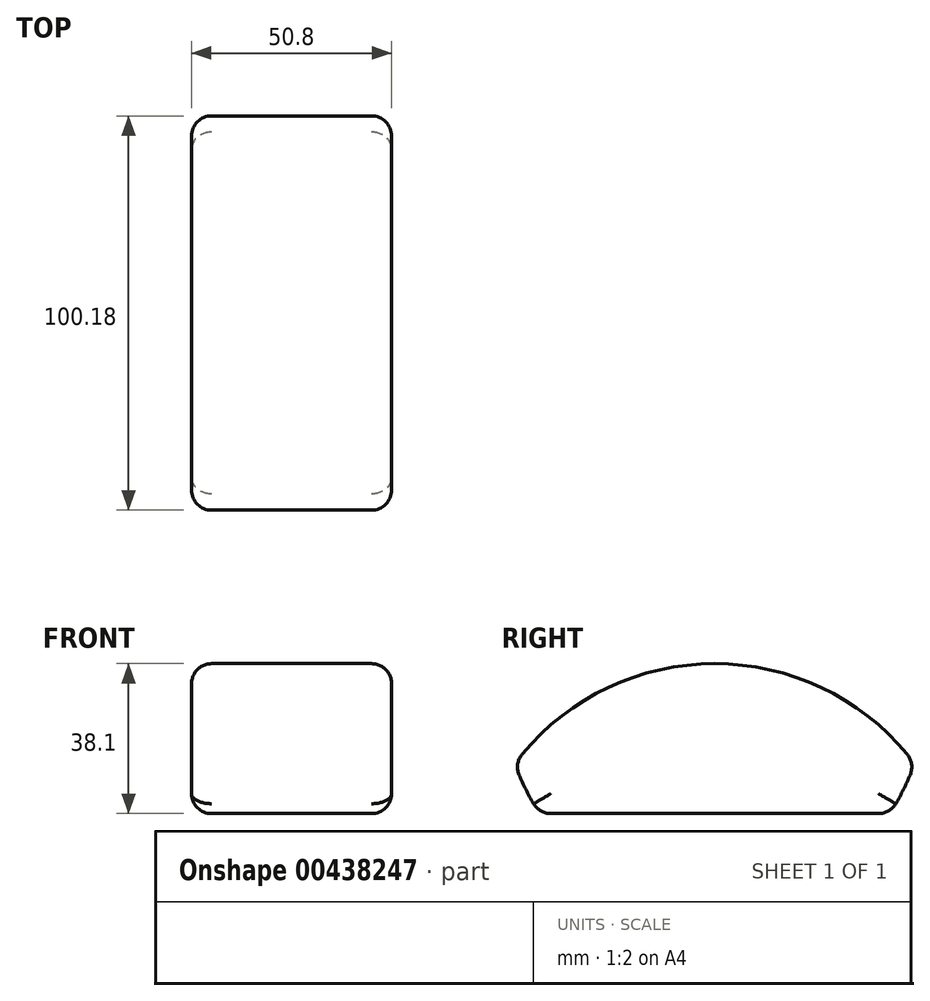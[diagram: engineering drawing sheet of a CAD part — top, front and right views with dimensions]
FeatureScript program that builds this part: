
annotation { "Feature Type Name" : "Feature", "Feature Type Description" : "" }
export const myFeature = defineFeature(function(context is Context, id is Id, definition is map)
    precondition{}
    {
        {
            var Q0;
            Q0=qCreatedBy(makeId("Right.planeOp"),FACE);
            var sketch = newSketch(context, id + "F0", { "sketchPlane" : qUnion([Q0])});
            skLineSegment(sketch, "E0", {"start": v(0, 0) * mm, "end": v(0, -12.7) * mm});
            skLineSegment(sketch, "E1", {"start": v(0, -12.7) * mm, "end": v(-44.45, -12.7) * mm});
            skLineSegment(sketch, "E2", {"start": v(0, -12.7) * mm, "end": v(44.45, -12.7) * mm});
            skLineSegment(sketch, "E3", {"start": v(0, 0) * mm, "end": v(-50.8, 0) * mm});
            skLineSegment(sketch, "E4", {"start": v(0, 0) * mm, "end": v(50.8, 0) * mm});
            skArc(sketch, "E5", {"start": v(-50.8, 0) * mm, "mid": v(-47.98, -6.53) * mm, "end": v(-44.45, -12.7) * mm});
            skArc(sketch, "E6", {"start": v(44.45, -12.7) * mm, "mid": v(47.98, -6.53) * mm, "end": v(50.8, 0) * mm});
            skLineSegment(sketch, "E7", {"start": v(0, 0) * mm, "end": v(0, 25.4) * mm});
            skLineSegment(sketch, "E8", {"start": v(50.8, 0) * mm, "end": v(6.35, 0) * mm});
            skArc(sketch, "E9", {"start": v(6.35, 0) * mm, "mid": v(4.15, 12.94) * mm, "end": v(0, 25.4) * mm});
            skArc(sketch, "E10", {"start": v(50.8, 0) * mm, "mid": v(28.4, 18.7) * mm, "end": v(0, 25.4) * mm});
            skArc(sketch, "E11", {"start": v(0, 25.4) * mm, "mid": v(-28.4, 18.7) * mm, "end": v(-50.8, 0) * mm});
            skSolve(sketch);
        }
        {
            var Q0;
            Q0 = qSketchRegion(id + "F0", true);
            extrude(context, id + "F1", {"entities" : qUnion([Q0]), "depth" : 25.4 * mm});
        }
        {
            var Q0;
            Q0 = qSketchRegion(id + "F0", true);
            extrude(context, id + "F2", {"entities" : qUnion([Q0]), "operationType" : NewBodyOperationType.ADD, "oppositeDirection" : true, "depth" : 25.4 * mm});
        }
        {
            var Q0;
            {var subQ0=sQuery(id+"F0.wireOp",EDGE,"E6");Q0=makeQuery(id+"F2.boolean.opBoolean","MERGE",FACE,{"derivedFrom":[makeQuery(id+"F1.opExtrude","SWEPT_FACE",FACE,{"disambiguationData":[OSD([subQ0])]}),makeQuery(id+"F2.opExtrude","SWEPT_FACE",FACE,{"disambiguationData":[OSD([subQ0])]})]});}
            var Q1;
            {var subQ0=sQuery(id+"F0.wireOp",EDGE,"E11");var subQ1=sQuery(id+"F0.wireOp",EDGE,"E10");Q1=makeQuery(id+"F2.boolean.opBoolean","MERGE",FACE,{"derivedFrom":[makeQuery(id+"F1.opExtrude","SWEPT_FACE",FACE,{"disambiguationData":[OSD([subQ1,subQ0])]}),makeQuery(id+"F2.opExtrude","SWEPT_FACE",FACE,{"disambiguationData":[OSD([subQ1,subQ0])]})]});}
            var Q2;
            {var subQ0=sQuery(id+"F0.wireOp",EDGE,"E5");Q2=makeQuery(id+"F2.boolean.opBoolean","MERGE",FACE,{"derivedFrom":[makeQuery(id+"F1.opExtrude","SWEPT_FACE",FACE,{"disambiguationData":[OSD([subQ0])]}),makeQuery(id+"F2.opExtrude","SWEPT_FACE",FACE,{"disambiguationData":[OSD([subQ0])]})]});}
            fillet(context, id + "F3", {"entities" : qUnion([Q0, Q1, Q2]), "radius" : 5.08 * mm, "tangentPropagation" : true, "allowEdgeOverflow" : false});
        }
        {
            var Q0;
            Q0=makeQuery(id+"F2.opExtrude","CAP_FACE",FACE,{"disambiguationData":[OSD([sQuery(id+"F0.wireOp",EDGE,"E1"),sQuery(id+"F0.wireOp",EDGE,"E2"),sQuery(id+"F0.wireOp",EDGE,"E5"),sQuery(id+"F0.wireOp",EDGE,"E6"),sQuery(id+"F0.wireOp",EDGE,"E10"),sQuery(id+"F0.wireOp",EDGE,"E11")])],"isStart":false});
            var Q1;
            Q1=makeQuery(id+"F1.opExtrude","CAP_FACE",FACE,{"disambiguationData":[OSD([sQuery(id+"F0.wireOp",EDGE,"E1"),sQuery(id+"F0.wireOp",EDGE,"E2"),sQuery(id+"F0.wireOp",EDGE,"E5"),sQuery(id+"F0.wireOp",EDGE,"E6"),sQuery(id+"F0.wireOp",EDGE,"E10"),sQuery(id+"F0.wireOp",EDGE,"E11")])],"isStart":false});
            fillet(context, id + "F4", {"entities" : qUnion([Q0, Q1]), "radius" : 5.08 * mm, "tangentPropagation" : true, "allowEdgeOverflow" : false});
        }
    });
